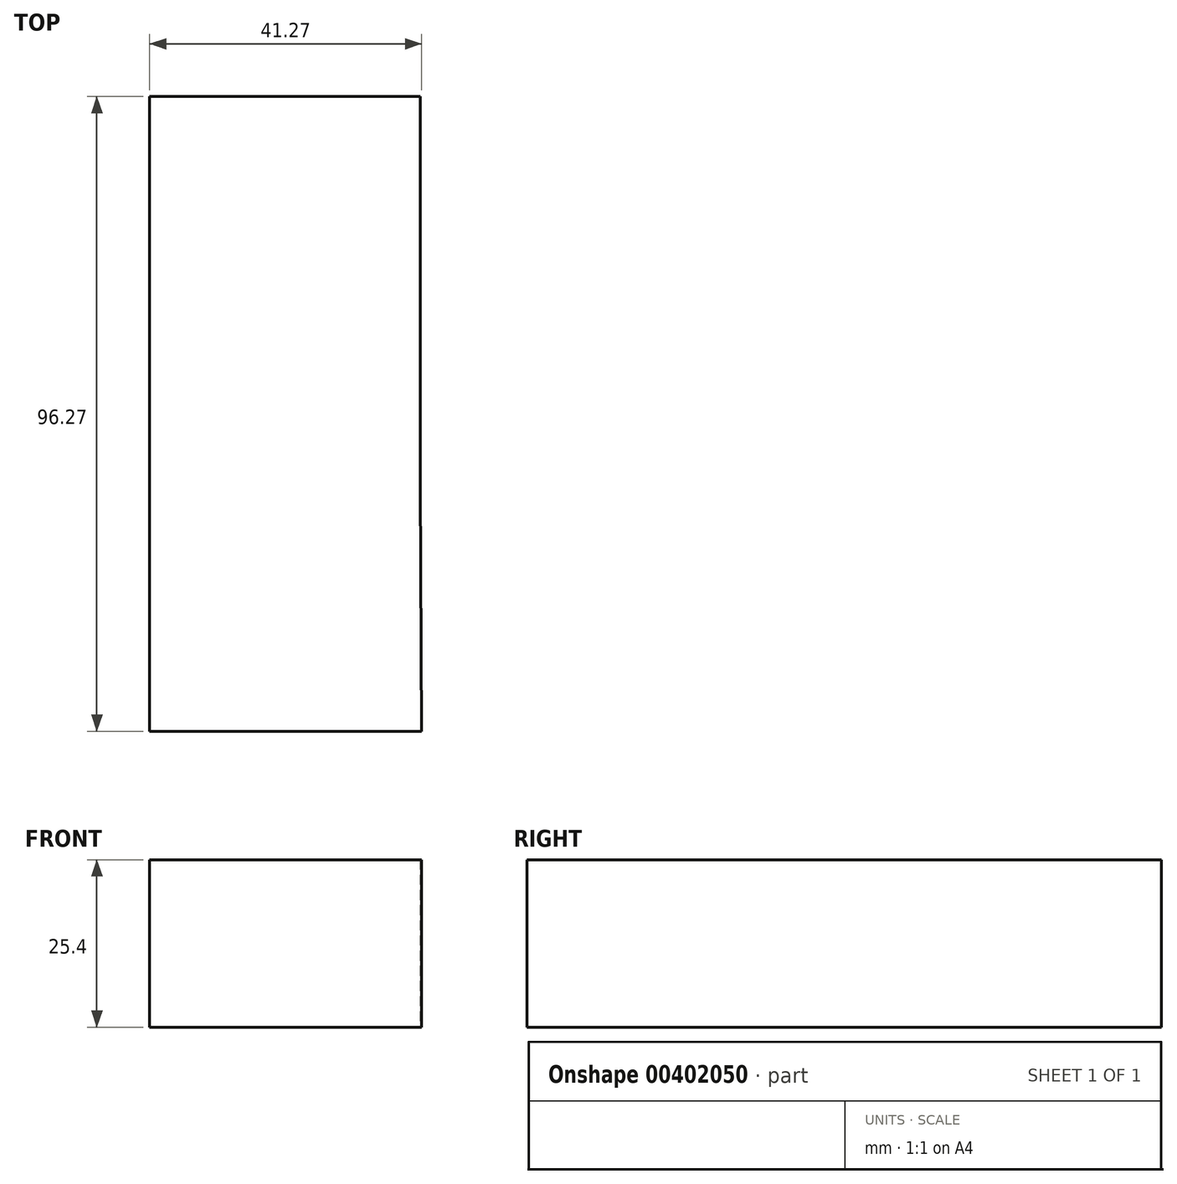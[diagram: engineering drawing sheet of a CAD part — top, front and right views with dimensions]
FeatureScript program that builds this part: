
annotation { "Feature Type Name" : "Feature", "Feature Type Description" : "" }
export const myFeature = defineFeature(function(context is Context, id is Id, definition is map)
    precondition{}
    {
        {
            var Q0;
            Q0=qCreatedBy(makeId("Top.planeOp"),FACE);
            var sketch = newSketch(context, id + "F0", { "sketchPlane" : qUnion([Q0])});
            skLineSegment(sketch, "E0", {"start": v(27.3, 41.15) * mm, "end": v(-13.76, 41.15) * mm});
            skLineSegment(sketch, "E1", {"start": v(-13.76, 41.15) * mm, "end": v(-13.76, 3.8) * mm});
            skLineSegment(sketch, "E2", {"start": v(-13.76, 3.8) * mm, "end": v(27.5, 3.8) * mm});
            skLineSegment(sketch, "E3", {"start": v(27.5, 3.8) * mm, "end": v(27.3, 41.15) * mm});
            skSolve(sketch);
        }
        {
            var Q0;
            Q0 = qSketchRegion(id + "F0", true);
            extrude(context, id + "F1", {"entities" : qUnion([Q0]), "depth" : 25.4 * mm});
        }
        {
            var Q0;
            Q0=makeQuery(id+"F1.opExtrude","SWEPT_FACE",FACE,{"disambiguationData":[OSD([sQuery(id+"F0.wireOp",EDGE,"E0")])]});
            var sketch = newSketch(context, id + "F2", { "sketchPlane" : qUnion([Q0])});
            skSolve(sketch);
        }
        {
            var Q0;
            {var subQ0=sQuery(id+"F0.wireOp",EDGE,"E0");Q0=makeQuery(id+"F2.imprint","IMPRINT",FACE,{"disambiguationData":[TD([[makeQuery(id+"F2.imprint","IMPRINT",EDGE,{"derivedFrom":makeQuery(id+"F1.opExtrude","CAP_EDGE",EDGE,{"disambiguationData":[OSD([subQ0])],"isStart":true})}),1.0]])]});}
            extrude(context, id + "F3", {"entities" : qUnion([Q0]), "operationType" : NewBodyOperationType.ADD, "depth" : 58.93 * mm});
        }
    });
